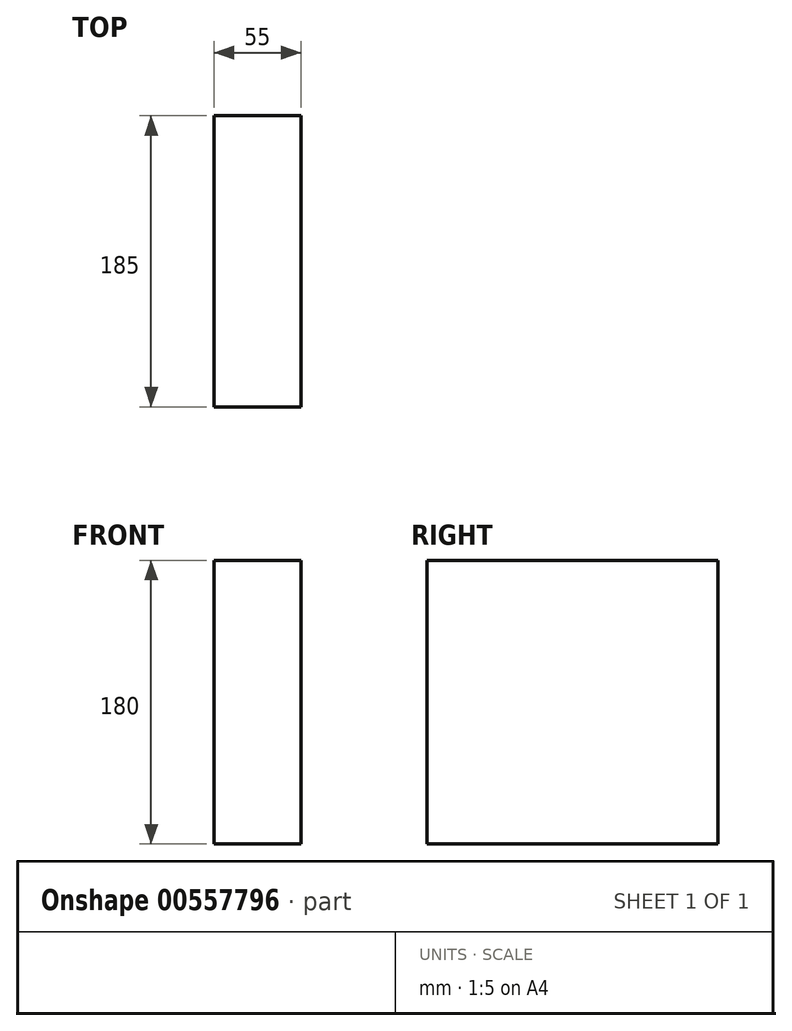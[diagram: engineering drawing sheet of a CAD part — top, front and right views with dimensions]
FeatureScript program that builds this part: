
annotation { "Feature Type Name" : "Feature", "Feature Type Description" : "" }
export const myFeature = defineFeature(function(context is Context, id is Id, definition is map)
    precondition{}
    {
        {
            var Q0;
            Q0=qCreatedBy(makeId("Front.planeOp"),FACE);
            var sketch = newSketch(context, id + "F0", { "sketchPlane" : qUnion([Q0])});
            skLineSegment(sketch, "E0.bottom", {"start": v(27.5, -90) * mm, "end": v(-27.5, -90) * mm});
            skLineSegment(sketch, "E0.top", {"start": v(27.5, 90) * mm, "end": v(-27.5, 90) * mm});
            skLineSegment(sketch, "E0.left", {"start": v(27.5, -90) * mm, "end": v(27.5, 90) * mm});
            skLineSegment(sketch, "E0.right", {"start": v(-27.5, -90) * mm, "end": v(-27.5, 90) * mm});
            skPoint(sketch, "E0.middle", {"position": v(0, 0) * mm});
            skSolve(sketch);
        }
        {
            var Q0;
            Q0=makeQuery(id+"F0.imprint","IMPRINT",FACE,{"disambiguationData":[TD([[makeQuery(id+"F0.imprint","IMPRINT",EDGE,{"derivedFrom":sQuery(id+"F0.wireOp",EDGE,"E0.bottom")}),-1.0]])]});
            extrude(context, id + "F1", {"entities" : qUnion([Q0]), "depth" : 185 * mm, "offsetDistance" : 25 * mm});
        }
    });
